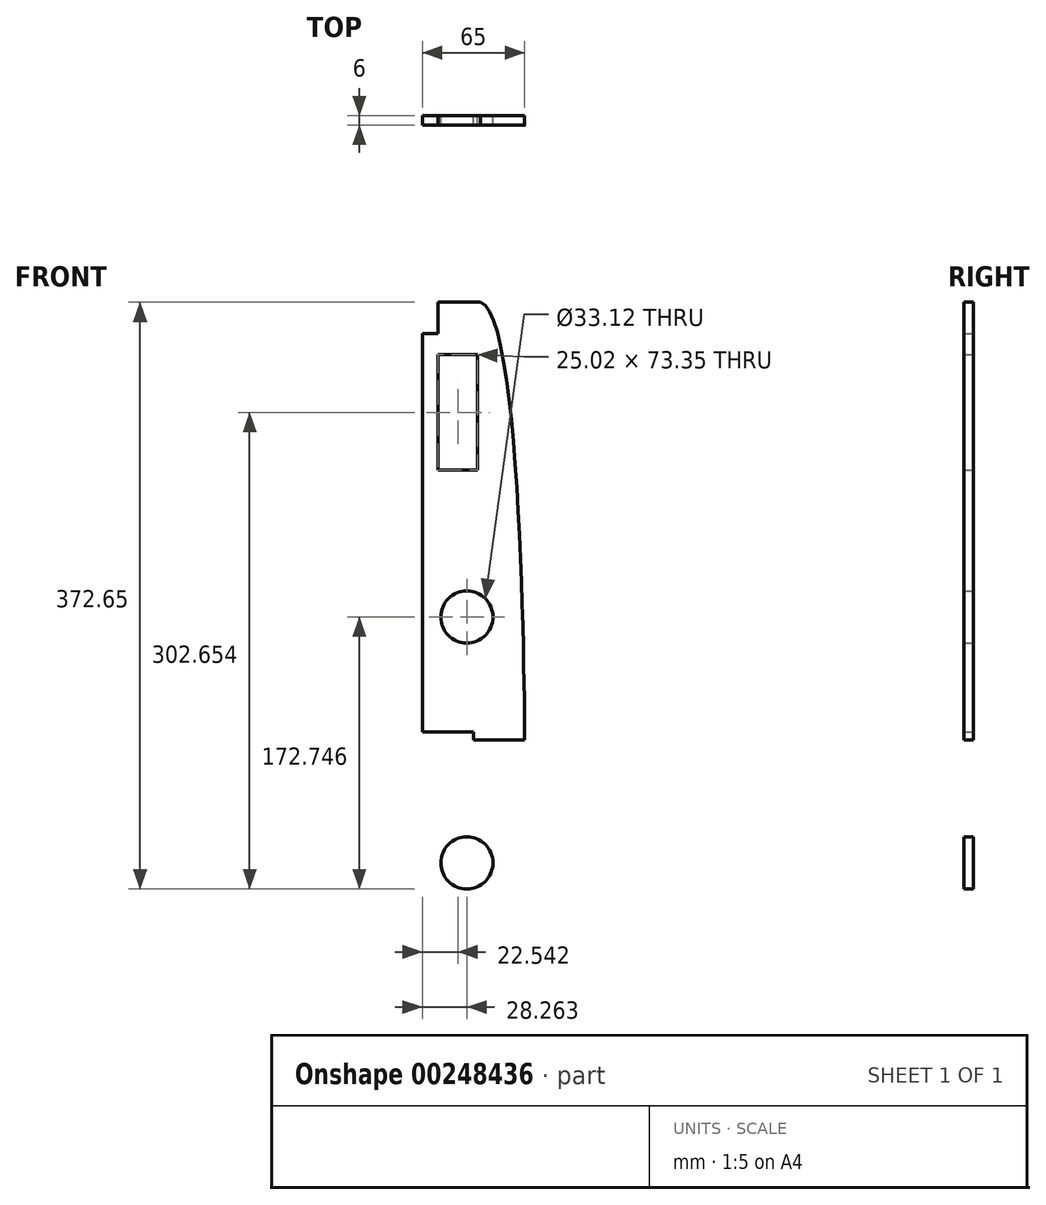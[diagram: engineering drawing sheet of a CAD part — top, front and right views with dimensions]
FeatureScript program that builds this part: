
annotation { "Feature Type Name" : "Feature", "Feature Type Description" : "" }
export const myFeature = defineFeature(function(context is Context, id is Id, definition is map)
    precondition{}
    {
        {
            var Q0;
            Q0=qCreatedBy(makeId("Front.planeOp"),FACE);
            var sketch = newSketch(context, id + "F0", { "sketchPlane" : qUnion([Q0])});
            skFitSpline(sketch, "E0", {"points": [v(248.93, 167.35) * mm, v(276.93, -110.65) * mm], "startDerivative": vector(83.51, -24.9) * mm, "endDerivative": vector(0.49, -7.2) * mm});
            skLineSegment(sketch, "E1", {"start": v(276.93, -110.65) * mm, "end": v(211.93, -110.65) * mm});
            skLineSegment(sketch, "E2", {"start": v(276.77, 167.35) * mm, "end": v(276.77, -108.25) * mm});
            skLineSegment(sketch, "E3.bottom", {"start": v(246.98, 134.03) * mm, "end": v(221.96, 134.03) * mm});
            skLineSegment(sketch, "E3.top", {"start": v(246.98, 60.68) * mm, "end": v(221.96, 60.68) * mm});
            skLineSegment(sketch, "E3.left", {"start": v(246.98, 134.03) * mm, "end": v(246.98, 60.68) * mm});
            skLineSegment(sketch, "E3.right", {"start": v(221.96, 134.03) * mm, "end": v(221.96, 60.68) * mm});
            skCircle(sketch, "E4", {"center": v(240.2, -32.55) * mm, "radius": 16.56 * mm});
            skCircle(sketch, "E5.MirrorC", {"center": v(240.2, -188.74) * mm, "radius": 16.56 * mm});
            skLineSegment(sketch, "E6.MirrorCS", {"start": v(276.77, -388.65) * mm, "end": v(276.77, -113.05) * mm});
            skLineSegment(sketch, "E7.MirrorCS", {"start": v(246.98, -355.32) * mm, "end": v(246.98, -281.97) * mm});
            skLineSegment(sketch, "E8.MirrorCS", {"start": v(246.98, -355.32) * mm, "end": v(221.96, -355.32) * mm});
            skFitSpline(sketch, "E9.MirrorCS", {"points": [v(248.93, -388.65) * mm, v(276.93, -110.65) * mm], "startDerivative": vector(83.51, 24.9) * mm, "endDerivative": vector(0.49, 7.2) * mm});
            skLineSegment(sketch, "E10.MirrorCS", {"start": v(276.77, -388.65) * mm, "end": v(221.93, -388.65) * mm});
            skLineSegment(sketch, "E11.MirrorCS", {"start": v(221.96, -355.32) * mm, "end": v(221.96, -281.97) * mm});
            skLineSegment(sketch, "E12.MirrorCS", {"start": v(246.98, -281.97) * mm, "end": v(221.96, -281.97) * mm});
            skLineSegment(sketch, "E13", {"start": v(244.43, -110.65) * mm, "end": v(244.43, -105.65) * mm});
            skLineSegment(sketch, "E14", {"start": v(244.43, -110.65) * mm, "end": v(244.43, -115.65) * mm});
            skLineSegment(sketch, "E15", {"start": v(244.43, -115.65) * mm, "end": v(211.93, -115.65) * mm});
            skLineSegment(sketch, "E16", {"start": v(244.43, -105.65) * mm, "end": v(211.93, -105.65) * mm});
            skLineSegment(sketch, "E17", {"start": v(221.93, 167.35) * mm, "end": v(221.93, 147.35) * mm});
            skLineSegment(sketch, "E18", {"start": v(221.93, 147.35) * mm, "end": v(211.93, 147.35) * mm});
            skLineSegment(sketch, "E19", {"start": v(221.93, 167.35) * mm, "end": v(248.93, 167.35) * mm});
            skLineSegment(sketch, "E20", {"start": v(211.93, 147.35) * mm, "end": v(211.93, -110.65) * mm});
            skLineSegment(sketch, "E21", {"start": v(221.93, 167.35) * mm, "end": v(221.93, 167.35) * mm});
            skLineSegment(sketch, "E22", {"start": v(248.93, 167.35) * mm, "end": v(276.77, 167.35) * mm});
            skLineSegment(sketch, "E23.MirrorCS", {"start": v(221.93, -388.65) * mm, "end": v(221.93, -368.65) * mm});
            skLineSegment(sketch, "E24.MirrorCS", {"start": v(221.93, -368.65) * mm, "end": v(211.93, -368.65) * mm});
            skLineSegment(sketch, "E25", {"start": v(221.93, -388.65) * mm, "end": v(248.93, -388.65) * mm});
            skLineSegment(sketch, "E26", {"start": v(211.93, -368.65) * mm, "end": v(211.93, -110.65) * mm});
            skSolve(sketch);
        }
        {
            var Q0;
            {var subQ3=sQuery(id+"F0.wireOp",EDGE,"c795efc6-8236-4691-9e25-113d5a84880f");Q0=makeQuery(id+"F0.imprint","IMPRINT",FACE,{"disambiguationData":[TD([[makeQuery(id+"F0.imprint","IMPRINT",EDGE,{"derivedFrom":subQ3}),-1.0]])]});}
            var Q1;
            Q1=makeQuery(id+"F0.imprint","IMPRINT",FACE,{"disambiguationData":[TD([[makeQuery(id+"F0.imprint","IMPRINT",EDGE,{"derivedFrom":sQuery(id+"F0.wireOp",EDGE,"E5.MirrorC")}),1.0]])]});
            var Q2;
            Q2=makeQuery(id+"F0.imprint","IMPRINT",FACE,{"disambiguationData":[TD([[makeQuery(id+"F0.imprint","IMPRINT",EDGE,{"derivedFrom":sQuery(id+"F0.wireOp",EDGE,"E3.bottom")}),-1.0]])]});
            extrude(context, id + "F1", {"entities" : qUnion([Q0, Q1, Q2]), "depth" : 6 * mm});
        }
    });
